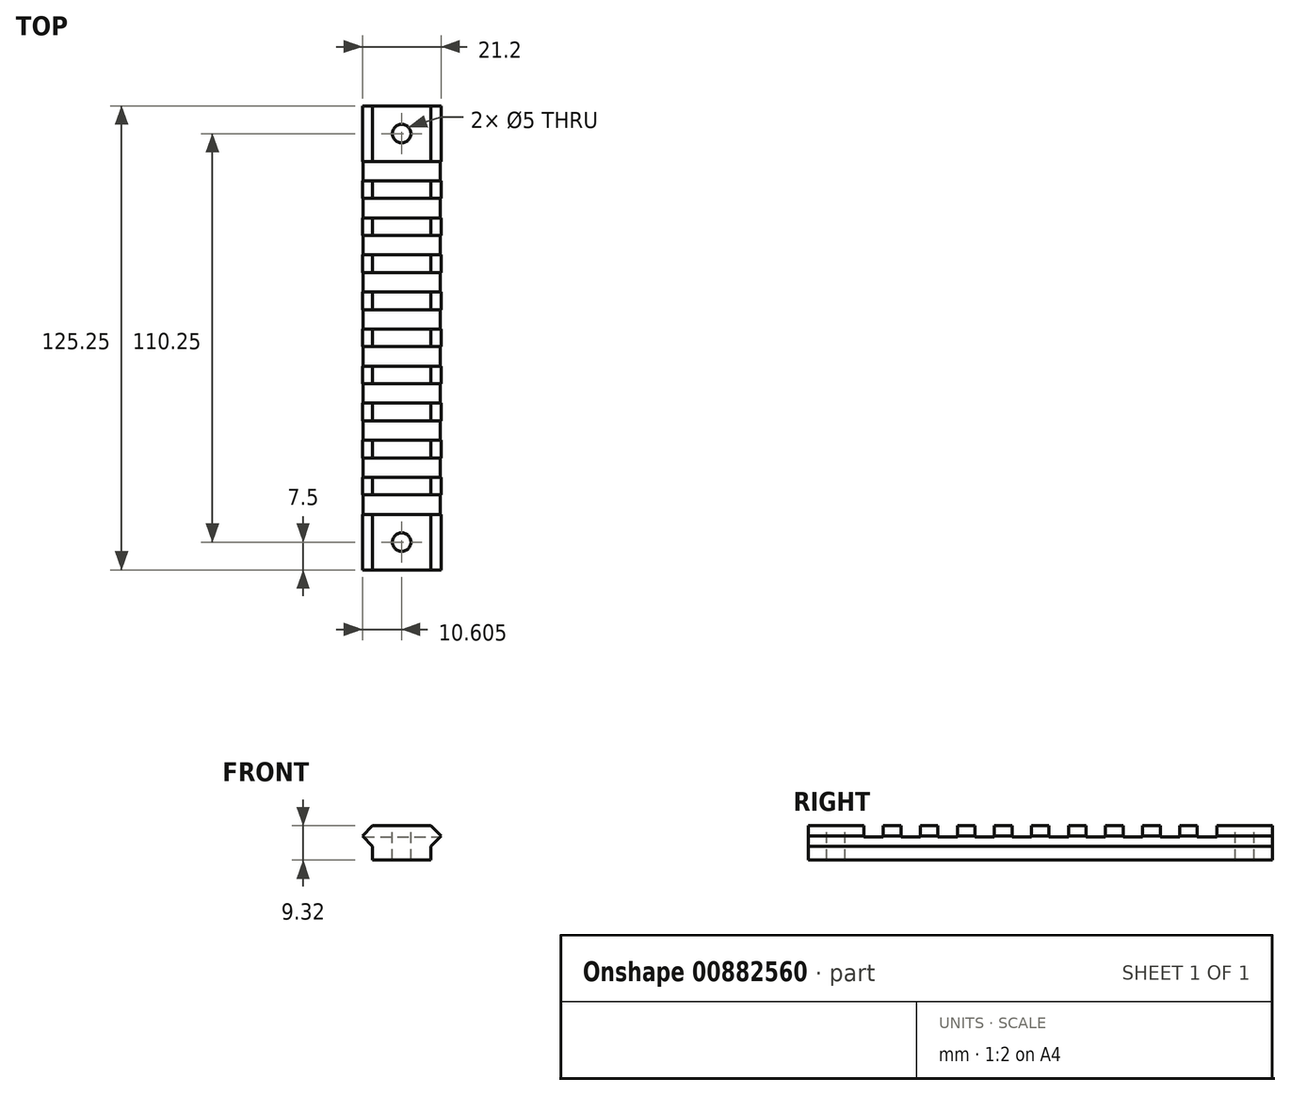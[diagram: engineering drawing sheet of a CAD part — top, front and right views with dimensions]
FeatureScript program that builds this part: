
annotation { "Feature Type Name" : "Feature", "Feature Type Description" : "" }
export const myFeature = defineFeature(function(context is Context, id is Id, definition is map)
    precondition{}
    {
        {
            var Q0;
            Q0=qCreatedBy(makeId("Front.planeOp"),FACE);
            var sketch = newSketch(context, id + "F0", { "sketchPlane" : qUnion([Q0])});
            skLineSegment(sketch, "E0", {"start": v(0, 0) * mm, "end": v(15.67, 0) * mm});
            skPoint(sketch, "E1", {"position": v(0, 9.32) * mm});
            skLineSegment(sketch, "E2", {"start": v(0, 9.32) * mm, "end": v(-2.77, 6.55) * mm});
            skLineSegment(sketch, "E3", {"start": v(0, 9.32) * mm, "end": v(15.67, 9.32) * mm});
            skLineSegment(sketch, "E4", {"start": v(-2.77, 6.56) * mm, "end": v(0, 3.8) * mm});
            skLineSegment(sketch, "E5", {"start": v(0, 3.8) * mm, "end": v(0, 0) * mm});
            skLineSegment(sketch, "E6", {"start": v(15.67, 9.32) * mm, "end": v(18.43, 6.56) * mm});
            skLineSegment(sketch, "E7", {"start": v(18.43, 6.56) * mm, "end": v(15.67, 3.8) * mm});
            skLineSegment(sketch, "E8", {"start": v(15.67, 3.8) * mm, "end": v(15.67, 0) * mm});
            skSolve(sketch);
        }
        {
            var Q0;
            Q0=makeQuery(id+"F0.imprint","IMPRINT",FACE,{"disambiguationData":[TD([[makeQuery(id+"F0.imprint","IMPRINT",EDGE,{"derivedFrom":sQuery(id+"F0.wireOp",EDGE,"E0")}),1.0]])]});
            extrude(context, id + "F1", {"entities" : qUnion([Q0]), "depth" : 125.25 * mm, "offsetDistance" : 25 * mm});
        }
        {
            var Q0;
            Q0=makeQuery(id+"F1.opExtrude","SWEPT_FACE",FACE,{"disambiguationData":[OSD([sQuery(id+"F0.wireOp",EDGE,"E3")])]});
            var sketch = newSketch(context, id + "F2", { "sketchPlane" : qUnion([Q0])});
            skLineSegment(sketch, "E9", {"start": v(-19.7, -15) * mm, "end": v(36.12, -15) * mm});
            skLineSegment(sketch, "E10", {"start": v(-19.7, -20.25) * mm, "end": v(36.12, -20.25) * mm});
            skLineSegment(sketch, "E11", {"start": v(-19.7, -15) * mm, "end": v(-19.7, -20.25) * mm});
            skLineSegment(sketch, "E12", {"start": v(36.12, -15) * mm, "end": v(36.12, -20.25) * mm});
            skPoint(sketch, "E13", {"position": v(-19.7, -25) * mm});
            skLineSegment(sketch, "E14.0.1.0", {"start": v(-19.7, -25) * mm, "end": v(36.12, -25) * mm});
            skLineSegment(sketch, "E14.0.1.1", {"start": v(-19.7, -25) * mm, "end": v(-19.7, -30.25) * mm});
            skPoint(sketch, "E14.0.1.2", {"position": v(-19.7, -35) * mm});
            skLineSegment(sketch, "E14.0.1.3", {"start": v(-19.7, -30.25) * mm, "end": v(36.12, -30.25) * mm});
            skLineSegment(sketch, "E14.0.1.4", {"start": v(36.12, -25) * mm, "end": v(36.12, -30.25) * mm});
            skLineSegment(sketch, "E14.0.2.0", {"start": v(-19.7, -35) * mm, "end": v(36.12, -35) * mm});
            skLineSegment(sketch, "E14.0.2.1", {"start": v(-19.7, -35) * mm, "end": v(-19.7, -40.25) * mm});
            skPoint(sketch, "E14.0.2.2", {"position": v(-19.7, -45) * mm});
            skLineSegment(sketch, "E14.0.2.3", {"start": v(-19.7, -40.25) * mm, "end": v(36.12, -40.25) * mm});
            skLineSegment(sketch, "E14.0.2.4", {"start": v(36.12, -35) * mm, "end": v(36.12, -40.25) * mm});
            skLineSegment(sketch, "E14.0.3.0", {"start": v(-19.7, -45) * mm, "end": v(36.12, -45) * mm});
            skLineSegment(sketch, "E14.0.3.1", {"start": v(-19.7, -45) * mm, "end": v(-19.7, -50.25) * mm});
            skPoint(sketch, "E14.0.3.2", {"position": v(-19.7, -55) * mm});
            skLineSegment(sketch, "E14.0.3.3", {"start": v(-19.7, -50.25) * mm, "end": v(36.12, -50.25) * mm});
            skLineSegment(sketch, "E14.0.3.4", {"start": v(36.12, -45) * mm, "end": v(36.12, -50.25) * mm});
            skLineSegment(sketch, "E14.0.4.0", {"start": v(-19.7, -55) * mm, "end": v(36.12, -55) * mm});
            skLineSegment(sketch, "E14.0.4.1", {"start": v(-19.7, -55) * mm, "end": v(-19.7, -60.25) * mm});
            skPoint(sketch, "E14.0.4.2", {"position": v(-19.7, -65) * mm});
            skLineSegment(sketch, "E14.0.4.3", {"start": v(-19.7, -60.25) * mm, "end": v(36.12, -60.25) * mm});
            skLineSegment(sketch, "E14.0.4.4", {"start": v(36.12, -55) * mm, "end": v(36.12, -60.25) * mm});
            skLineSegment(sketch, "E14.0.5.0", {"start": v(-19.7, -65) * mm, "end": v(36.12, -65) * mm});
            skLineSegment(sketch, "E14.0.5.1", {"start": v(-19.7, -65) * mm, "end": v(-19.7, -70.25) * mm});
            skPoint(sketch, "E14.0.5.2", {"position": v(-19.7, -75) * mm});
            skLineSegment(sketch, "E14.0.5.3", {"start": v(-19.7, -70.25) * mm, "end": v(36.12, -70.25) * mm});
            skLineSegment(sketch, "E14.0.5.4", {"start": v(36.12, -65) * mm, "end": v(36.12, -70.25) * mm});
            skLineSegment(sketch, "E14.0.6.0", {"start": v(-19.7, -75) * mm, "end": v(36.12, -75) * mm});
            skLineSegment(sketch, "E14.0.6.1", {"start": v(-19.7, -75) * mm, "end": v(-19.7, -80.25) * mm});
            skPoint(sketch, "E14.0.6.2", {"position": v(-19.7, -85) * mm});
            skLineSegment(sketch, "E14.0.6.3", {"start": v(-19.7, -80.25) * mm, "end": v(36.12, -80.25) * mm});
            skLineSegment(sketch, "E14.0.6.4", {"start": v(36.12, -75) * mm, "end": v(36.12, -80.25) * mm});
            skLineSegment(sketch, "E14.0.7.0", {"start": v(-19.7, -85) * mm, "end": v(36.12, -85) * mm});
            skLineSegment(sketch, "E14.0.7.1", {"start": v(-19.7, -85) * mm, "end": v(-19.7, -90.25) * mm});
            skPoint(sketch, "E14.0.7.2", {"position": v(-19.7, -95) * mm});
            skLineSegment(sketch, "E14.0.7.3", {"start": v(-19.7, -90.25) * mm, "end": v(36.12, -90.25) * mm});
            skLineSegment(sketch, "E14.0.7.4", {"start": v(36.12, -85) * mm, "end": v(36.12, -90.25) * mm});
            skLineSegment(sketch, "E14.0.8.0", {"start": v(-19.7, -95) * mm, "end": v(36.12, -95) * mm});
            skLineSegment(sketch, "E14.0.8.1", {"start": v(-19.7, -95) * mm, "end": v(-19.7, -100.25) * mm});
            skPoint(sketch, "E14.0.8.2", {"position": v(-19.7, -105) * mm});
            skLineSegment(sketch, "E14.0.8.3", {"start": v(-19.7, -100.25) * mm, "end": v(36.12, -100.25) * mm});
            skLineSegment(sketch, "E14.0.8.4", {"start": v(36.12, -95) * mm, "end": v(36.12, -100.25) * mm});
            skLineSegment(sketch, "E14.0.9.0", {"start": v(-19.7, -105) * mm, "end": v(36.12, -105) * mm});
            skLineSegment(sketch, "E14.0.9.1", {"start": v(-19.7, -105) * mm, "end": v(-19.7, -110.25) * mm});
            skPoint(sketch, "E14.0.9.2", {"position": v(-19.7, -115) * mm});
            skLineSegment(sketch, "E14.0.9.3", {"start": v(-19.7, -110.25) * mm, "end": v(36.12, -110.25) * mm});
            skLineSegment(sketch, "E14.0.9.4", {"start": v(36.12, -105) * mm, "end": v(36.12, -110.25) * mm});
            skLineSegment(sketch, "E14.direction1", {"start": v(-19.7, -15) * mm, "end": v(12.9, -15) * mm, "construction": true});
            skLineSegment(sketch, "E14.direction2", {"start": v(-19.7, -15) * mm, "end": v(-19.7, -25) * mm, "construction": true});
            skSolve(sketch);
        }
        {
            var Q0;
            Q0=qSketchRegion(id+"F2",true);
            extrude(context, id + "F3", {"entities" : qUnion([Q0]), "operationType" : NewBodyOperationType.REMOVE, "oppositeDirection" : true, "depth" : 3 * mm, "offsetDistance" : 25 * mm});
        }
        {
            var Q0;
            {var subQ1=sQuery(id+"F0.wireOp",EDGE,"E3");var subQ6=makeQuery(id+"F1.opExtrude","CAP_EDGE",EDGE,{"disambiguationData":[OSD([subQ1])],"isStart":true});Q0=makeQuery(id+"F2.imprint","IMPRINT",FACE,{"disambiguationData":[TD([[makeQuery(id+"F2.imprint","IMPRINT",EDGE,{"derivedFrom":subQ6}),-1.0]])]});}
            var sketch = newSketch(context, id + "F4", { "sketchPlane" : qUnion([Q0])});
            skPoint(sketch, "E15", {"position": v(7.83, -7.5) * mm});
            skCircle(sketch, "E16", {"center": v(7.83, -7.5) * mm, "radius": 2.5 * mm});
            skPoint(sketch, "E17", {"position": v(7.84, -117.75) * mm});
            skCircle(sketch, "E18", {"center": v(7.84, -117.75) * mm, "radius": 2.5 * mm});
            skSolve(sketch);
        }
        {
            var Q0;
            Q0=qSketchRegion(id+"F4",true);
            extrude(context, id + "F5", {"entities" : qUnion([Q0]), "operationType" : NewBodyOperationType.REMOVE, "oppositeDirection" : true, "depth" : 25 * mm, "offsetDistance" : 25 * mm});
        }
    });
